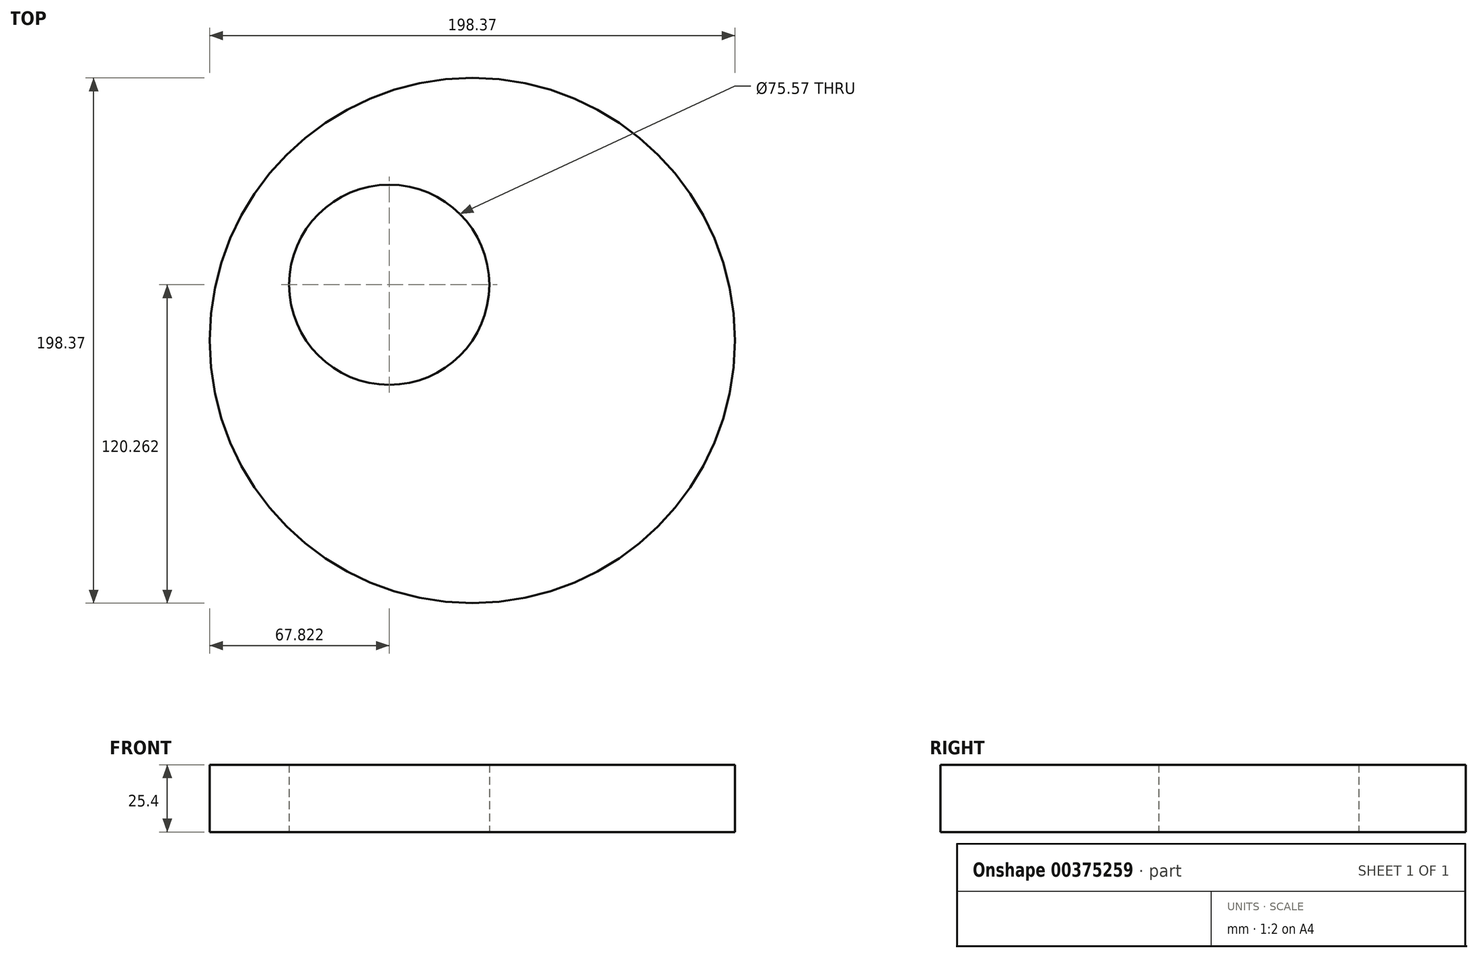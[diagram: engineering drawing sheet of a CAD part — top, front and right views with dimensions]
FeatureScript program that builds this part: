
annotation { "Feature Type Name" : "Feature", "Feature Type Description" : "" }
export const myFeature = defineFeature(function(context is Context, id is Id, definition is map)
    precondition{}
    {
        {
            var Q0;
            Q0=qCreatedBy(makeId("Top.planeOp"),FACE);
            var sketch = newSketch(context, id + "F0", { "sketchPlane" : qUnion([Q0])});
            skCircle(sketch, "E0", {"center": v(-33.04, 59.44) * mm, "radius": 37.79 * mm});
            skCircle(sketch, "E1", {"center": v(-1.67, 38.37) * mm, "radius": 99.18 * mm});
            skSolve(sketch);
        }
        {
            var Q0;
            Q0 = qSketchRegion(id + "F0", true);
            extrude(context, id + "F1", {"entities" : qUnion([Q0]), "depth" : 25.4 * mm});
        }
    });
